# Revit family: Panel de control de extinción_Aguilera Electronica
name_source: partatom
category: Equipos eléctricos
revit_build: Autodesk Revit 2017 (Build: 20160225_1515(x64)
units: mm (PartAtom-declared; Revit-internal decimal feet)

## family parameters
Anfitrión = Cara
Compartido = No
Configuración de panel = Dos columnas, circuitos en horizontal
Corte con vacíos al cargar = No
Cota de conector redondo = Diámetro de uso
Número OmniClass = 23.85.30.21.11.14
Punto de cálculo de habitación = No
Tipo de pieza = Cuadro de control
Título OmniClass = Alarm Panels

## types (2) — shared parameters
Alto = 272 mm  [stored 0.892388 ft]
Ancho = 320 mm  [stored 1.04987 ft]
Descripción = Desarrollado y fabricado por Aguilera Electrónica según Norma UNE EN12094-1
Características:
• 2 zonas de detección supervisadas.
• Modo de funcionamiento programable como:
• Doble detección: Dos alarmas en una zona.
• Detección cruzada: Una alarma en cada zona.
• Mixta: Dos alarmas en el panel.
• Zona de detección supervisada para pulsador de disparo de extinción.
• Entrada supervisada para pulsador de paro de extinción.
• Pulsadores de disparo y paro de extinción incorporados en el panel.
• 2 Entradas vigiladas independientes para supervisión de presostato o control de pesaje y control de flujo.
• Salida vigilada de evacuación y salida para cartel de disparo.
• Llave de selección de modo: automático, manual o desarmado.
• Display con indicación del tiempo restante para la descarga.
• Tiempo de salida antes de la extinción programable entre 0 y 60 segundos.
• Integrable en el sistema algorítmico.
• Relés opcionales para repetir los estados de la central.
• Dimensiones: 320 x 272 x 125 mm.
• Puede alojar 2 baterías de 12V/7Ah.
• Equipa una tarjeta microprocesada que mantiene informada a la central algorítmica de su estado
permanentemente.
Diámetro tubo = 20 mm  [stored 0.0656168 ft]
Elevación por defecto = 1200 mm
Fabricante = Aguilera Electrónica
Fondo = 125 mm  [stored 0.410105 ft]
Potencia aparente = 460 VA
Potencial eléctrico = 230 V
Símbolo = Sí
Símbolo texto modelo = Sí
URL = http://aguilera.es

## per-type parameters (varying)
| type | Comentarios de tipo | Modelo |
| Panel de control de extinción con tarjeta de integración | Con tarjeta de integración | AE/SA-PX2 |
| Panel de control de extinción para detectores C5, con tarjeta de integración | Para detectores C5, con tarjeta de integración | AE/SA-PX2C5 |

note: [stored X ft] marks values corroborated as IEEE doubles in the binary element streams (Revit-internal decimal feet)
